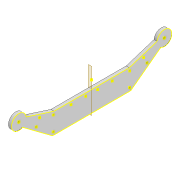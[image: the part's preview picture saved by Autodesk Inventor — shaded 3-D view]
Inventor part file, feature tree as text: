
AUTODESK INVENTOR PART (.ipt)
format: ipt  version: 2022 (Build 260153000, 153)  size: 247,808 bytes
history: native  units: mm
features: sketch x2, extrude x1, projected_geometry x1
ambient origin geometry x8: Origin, YZ Plane, XZ Plane, XY Plane, X Axis, Y Axis, Z Axis, Center Point
bodies: Solid1 (feature_tree)
feature tree (4):
  extrude  "Extrusion1"  Depth=3.9mm
  sketch  "Sketch8"  dims[d6=5.0mm d7=0.0mm d25=3.0mm d28=3.0mm d43=59.0mm d44=65.0mm d45=65.0mm d47=59.0mm d48=10.0mm d49=10.0mm d50=10.0mm d52=14.0mm d53=3.0mm d54=3.0mm d55=4.0mm d56=4.0mm d57=25.0mm d58=25.0mm d59=10.0mm d60=10.0mm d61=10.0mm d62=3.0mm d63=3.0mm d64=3.0mm d65=3.0mm d66=3.0mm d67=10.0mm d68=25.0mm d69=3.0mm d70=3.0mm d71=10.0mm d72=25.0mm d73=25.0mm d74=25.0mm d76=3.0mm d78=3.0mm d79=3.0mm d80=3.0mm d81=6.0mm d82=6.0mm d83=2.0mm]
  sketch  "Sketch1"  dims[d2=3.9mm d4=3.9mm]
  projected_geometry  "Project Cut Edges1"
